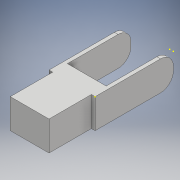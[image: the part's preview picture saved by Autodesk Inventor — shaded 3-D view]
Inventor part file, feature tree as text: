
AUTODESK INVENTOR PART (.ipt)
format: ipt  version: 2017 (Build 210142000, 142)  size: 130,048 bytes
history: native  units: mm
features: sketch x6, extrude x3, other x1, fillet x1
ambient origin geometry x8: Origin, YZ Plane, XZ Plane, XY Plane, X Axis, Y Axis, Z Axis, Center Point
bodies: Body1 (feature_tree)
feature tree (11):
  other  "ソリッド1"
  extrude  "押し出し1"  Depth=0.04mm
  extrude  "押し出し2"  Depth=0.32mm
  sketch  "スケッチ3"
  extrude  "押し出し3"  Depth=0.69mm TaperAngle=0.0deg
  fillet  "フィレット1"  Radius=0.04mm
  sketch  "スケッチ5"
  sketch  "スケッチ6"
  sketch  "スケッチ1"
  sketch  "スケッチ2"
  sketch  "スケッチ4"
